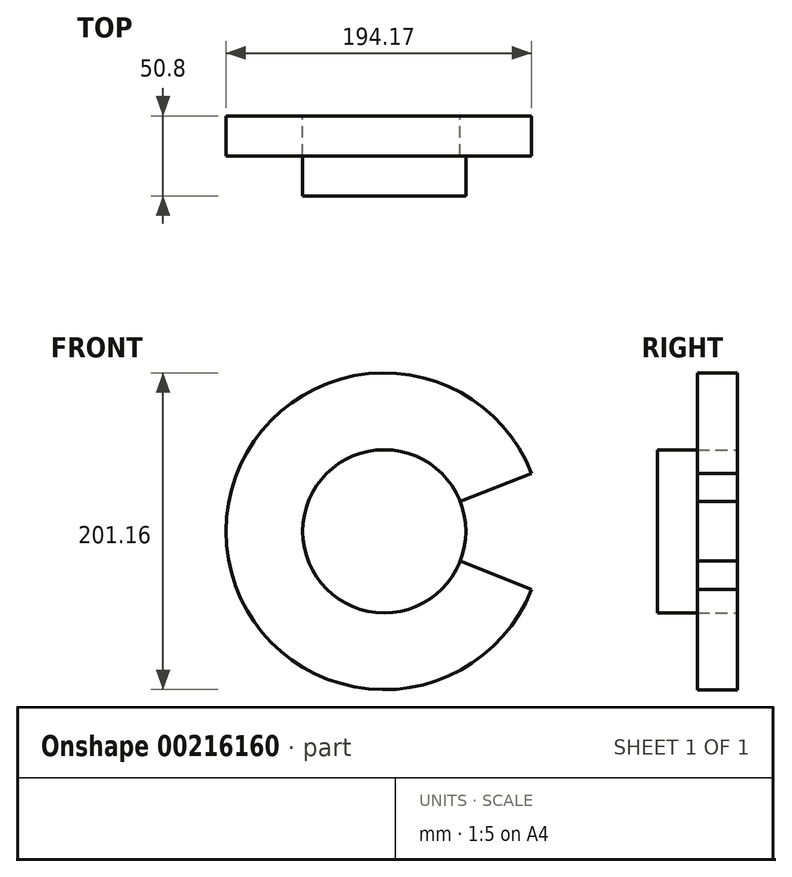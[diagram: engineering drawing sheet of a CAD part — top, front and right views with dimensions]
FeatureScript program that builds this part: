
annotation { "Feature Type Name" : "Feature", "Feature Type Description" : "" }
export const myFeature = defineFeature(function(context is Context, id is Id, definition is map)
    precondition{}
    {
        {
            var Q0;
            Q0=qCreatedBy(makeId("Front.planeOp"),FACE);
            var sketch = newSketch(context, id + "F0", { "sketchPlane" : qUnion([Q0])});
            skArc(sketch, "E0", {"start": v(93.6, 36.85) * mm, "mid": v(-100.58, 0) * mm, "end": v(93.6, -36.85) * mm});
            skCircle(sketch, "E1", {"center": v(0, 0) * mm, "radius": 51.82 * mm});
            skLineSegment(sketch, "E2", {"start": v(0, 0) * mm, "end": v(93.6, 36.85) * mm, "construction": true});
            skLineSegment(sketch, "E3", {"start": v(0, 0) * mm, "end": v(93.6, -36.85) * mm, "construction": true});
            skLineSegment(sketch, "E4", {"start": v(0, 0) * mm, "end": v(100.58, 0) * mm, "construction": true});
            skLineSegment(sketch, "E5", {"start": v(48.21, 18.98) * mm, "end": v(93.6, 36.85) * mm});
            skLineSegment(sketch, "E6", {"start": v(48.21, -18.98) * mm, "end": v(93.6, -36.85) * mm});
            skSolve(sketch);
        }
        {
            var Q0;
            Q0=makeQuery(id+"F0.imprint","IMPRINT",FACE,{"disambiguationData":[TD([[makeQuery(id+"F0.imprint","IMPRINT",EDGE,{"derivedFrom":sQuery(id+"F0.wireOp",EDGE,"E0")}),1.0]])]});
            extrude(context, id + "F1", {"entities" : qUnion([Q0]), "depth" : 25.4 * mm});
        }
        {
            var Q0;
            Q0=makeQuery(id+"F1.opExtrude","CAP_FACE",FACE,{"disambiguationData":[OSD([sQuery(id+"F0.wireOp",EDGE,"E0"),sQuery(id+"F0.wireOp",EDGE,"E1"),sQuery(id+"F0.wireOp",EDGE,"E5"),sQuery(id+"F0.wireOp",EDGE,"E6")])],"isStart":false});
            var sketch = newSketch(context, id + "F2", { "sketchPlane" : qUnion([Q0])});
            skCircle(sketch, "E7", {"center": v(0, 0) * mm, "radius": 51.82 * mm});
            skSolve(sketch);
        }
        {
            var Q0;
            Q0 = qSketchRegion(id + "F2", true);
            extrude(context, id + "F3", {"entities" : qUnion([Q0]), "depth" : 25.4 * mm});
        }
    });
